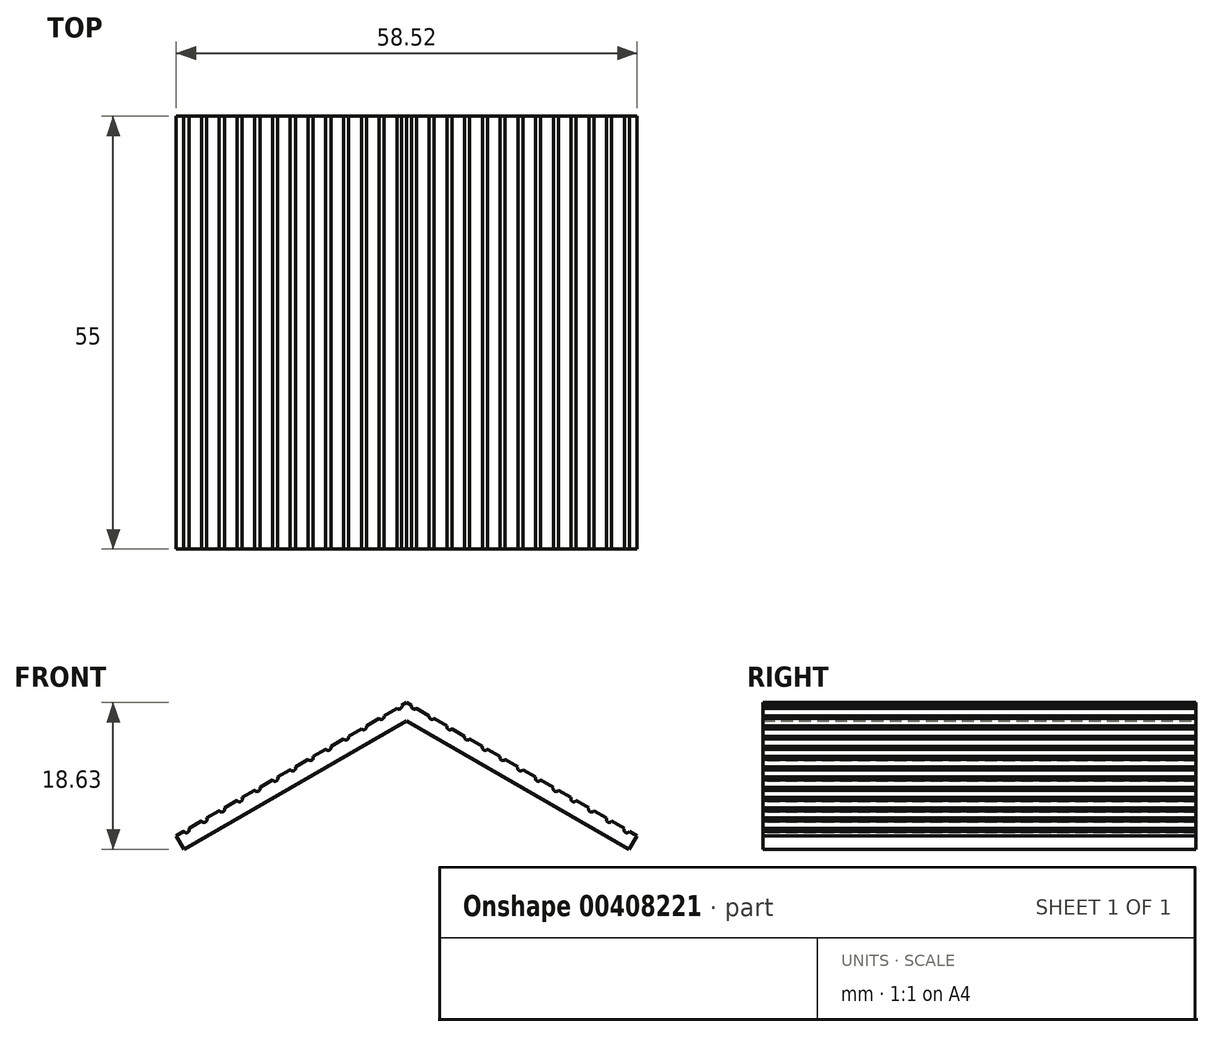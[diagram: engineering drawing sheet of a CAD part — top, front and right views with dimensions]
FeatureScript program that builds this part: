
annotation { "Feature Type Name" : "Feature", "Feature Type Description" : "" }
export const myFeature = defineFeature(function(context is Context, id is Id, definition is map)
    precondition{}
    {
        {
            var Q0;
            Q0=qCreatedBy(makeId("Front.planeOp"),FACE);
            var sketch = newSketch(context, id + "F0", { "sketchPlane" : qUnion([Q0])});
            skLineSegment(sketch, "E0", {"start": v(0, 39.37) * mm, "end": v(-28.28, 23.05) * mm});
            skLineSegment(sketch, "E1", {"start": v(-22.5, 26.38) * mm, "end": v(0, 26.38) * mm, "construction": true});
            skLineSegment(sketch, "E2.0", {"start": v(0, 41.68) * mm, "end": v(-29.26, 24.79) * mm});
            skLineSegment(sketch, "E3", {"start": v(-29.26, 24.79) * mm, "end": v(-28.28, 23.05) * mm});
            skLineSegment(sketch, "E4", {"start": v(0, 39.37) * mm, "end": v(0, 41.68) * mm});
            skLineSegment(sketch, "E5.MirrorCS", {"start": v(29.26, 24.79) * mm, "end": v(28.28, 23.05) * mm});
            skLineSegment(sketch, "E6.MirrorCS", {"start": v(0, 39.37) * mm, "end": v(28.28, 23.05) * mm});
            skLineSegment(sketch, "E7.MirrorCS", {"start": v(0, 41.68) * mm, "end": v(29.26, 24.79) * mm});
            skSolve(sketch);
        }
        {
            var Q0;
            Q0 = qSketchRegion(id + "F0", true);
            extrude(context, id + "F1", {"entities" : qUnion([Q0]), "depth" : 55 * mm});
        }
        {
            var Q0;
            Q0=makeQuery(id+"F1.opExtrude","CAP_FACE",FACE,{"disambiguationData":[OSD([sQuery(id+"F0.wireOp",EDGE,"E0"),sQuery(id+"F0.wireOp",EDGE,"E2.0"),sQuery(id+"F0.wireOp",EDGE,"E3"),sQuery(id+"F0.wireOp",EDGE,"E5.MirrorCS"),sQuery(id+"F0.wireOp",EDGE,"E6.MirrorCS"),sQuery(id+"F0.wireOp",EDGE,"E7.MirrorCS")])],"isStart":false});
            var sketch = newSketch(context, id + "F2", { "sketchPlane" : qUnion([Q0])});
            skCircle(sketch, "E8", {"center": v(-27.98, 25.52) * mm, "radius": 0.37 * mm});
            skCircle(sketch, "E9.1.0.0", {"center": v(-25.73, 26.83) * mm, "radius": 0.37 * mm});
            skCircle(sketch, "E9.2.0.0", {"center": v(-23.48, 28.14) * mm, "radius": 0.37 * mm});
            skCircle(sketch, "E9.3.0.0", {"center": v(-21.23, 29.45) * mm, "radius": 0.37 * mm});
            skCircle(sketch, "E9.4.0.0", {"center": v(-18.98, 30.76) * mm, "radius": 0.37 * mm});
            skCircle(sketch, "E9.5.0.0", {"center": v(-16.73, 32.06) * mm, "radius": 0.37 * mm});
            skCircle(sketch, "E9.6.0.0", {"center": v(-14.48, 33.37) * mm, "radius": 0.37 * mm});
            skCircle(sketch, "E9.7.0.0", {"center": v(-12.23, 34.68) * mm, "radius": 0.37 * mm});
            skCircle(sketch, "E9.8.0.0", {"center": v(-9.98, 35.99) * mm, "radius": 0.37 * mm});
            skCircle(sketch, "E9.9.0.0", {"center": v(-7.73, 37.3) * mm, "radius": 0.37 * mm});
            skCircle(sketch, "E9.10.0.0", {"center": v(-5.48, 38.6) * mm, "radius": 0.37 * mm});
            skCircle(sketch, "E9.11.0.0", {"center": v(-3.23, 39.91) * mm, "radius": 0.37 * mm});
            skCircle(sketch, "E9.12.0.0", {"center": v(-0.98, 41.22) * mm, "radius": 0.37 * mm});
            skCircle(sketch, "E9.13.0.0", {"center": v(1.28, 42.53) * mm, "radius": 0.37 * mm});
            skCircle(sketch, "E9.14.0.0", {"center": v(3.53, 43.84) * mm, "radius": 0.37 * mm});
            skLineSegment(sketch, "E10", {"start": v(0, 41.68) * mm, "end": v(0, 37.22) * mm, "construction": true});
            skCircle(sketch, "E11.MirrorC", {"center": v(7.73, 37.3) * mm, "radius": 0.37 * mm});
            skCircle(sketch, "E12.MirrorC", {"center": v(27.98, 25.52) * mm, "radius": 0.37 * mm});
            skCircle(sketch, "E13.MirrorC", {"center": v(12.23, 34.68) * mm, "radius": 0.37 * mm});
            skCircle(sketch, "E14.MirrorC", {"center": v(25.73, 26.83) * mm, "radius": 0.37 * mm});
            skCircle(sketch, "E15.MirrorC", {"center": v(-1.28, 42.53) * mm, "radius": 0.37 * mm});
            skCircle(sketch, "E16.MirrorC", {"center": v(18.98, 30.76) * mm, "radius": 0.37 * mm});
            skCircle(sketch, "E17.MirrorC", {"center": v(0.98, 41.22) * mm, "radius": 0.37 * mm});
            skCircle(sketch, "E18.MirrorC", {"center": v(21.23, 29.45) * mm, "radius": 0.37 * mm});
            skCircle(sketch, "E19.MirrorC", {"center": v(16.73, 32.06) * mm, "radius": 0.37 * mm});
            skCircle(sketch, "E20.MirrorC", {"center": v(23.48, 28.14) * mm, "radius": 0.37 * mm});
            skCircle(sketch, "E21.MirrorC", {"center": v(3.23, 39.91) * mm, "radius": 0.37 * mm});
            skCircle(sketch, "E22.MirrorC", {"center": v(5.48, 38.6) * mm, "radius": 0.37 * mm});
            skCircle(sketch, "E23.MirrorC", {"center": v(14.48, 33.37) * mm, "radius": 0.37 * mm});
            skCircle(sketch, "E24.MirrorC", {"center": v(9.98, 35.99) * mm, "radius": 0.37 * mm});
            skCircle(sketch, "E25.MirrorC", {"center": v(-3.53, 43.84) * mm, "radius": 0.37 * mm});
            skSolve(sketch);
        }
        {
            var Q0;
            Q0 = qSketchRegion(id + "F2", true);
            extrude(context, id + "F3", {"entities" : qUnion([Q0]), "operationType" : NewBodyOperationType.REMOVE, "oppositeDirection" : true, "depth" : 63.7 * mm});
        }
    });
